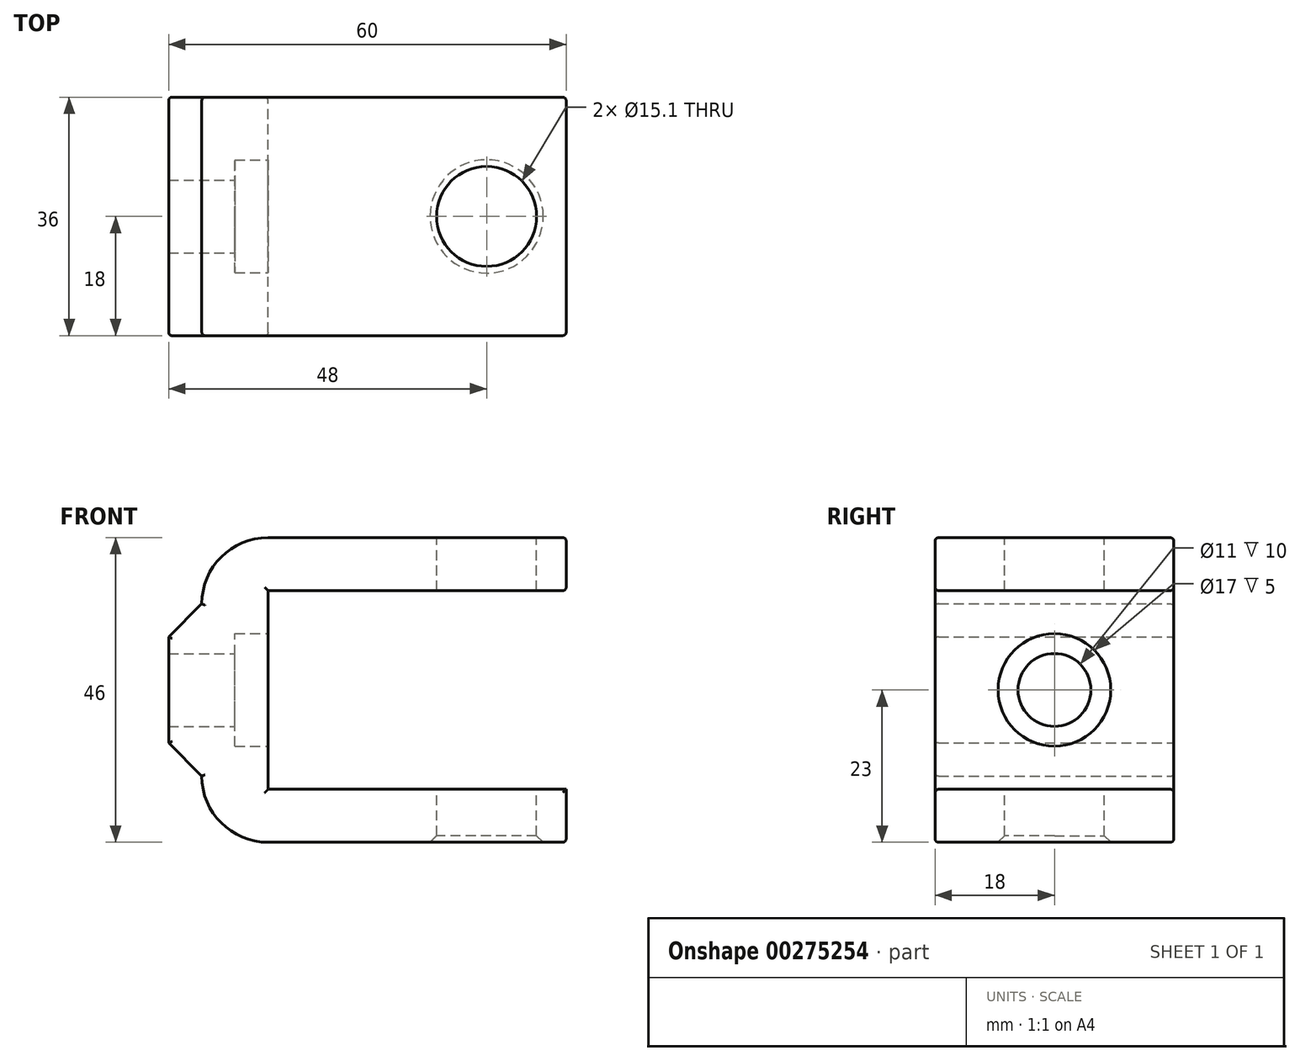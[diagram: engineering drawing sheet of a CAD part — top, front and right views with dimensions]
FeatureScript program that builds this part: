
annotation { "Feature Type Name" : "Feature", "Feature Type Description" : "" }
export const myFeature = defineFeature(function(context is Context, id is Id, definition is map)
    precondition{}
    {
        {
            var Q0;
            Q0=qCreatedBy(makeId("Front.planeOp"),FACE);
            var sketch = newSketch(context, id + "F0", { "sketchPlane" : qUnion([Q0])});
            skLineSegment(sketch, "E0", {"start": v(-43.93, 0) * mm, "end": v(68.64, 0) * mm, "construction": true});
            skLineSegment(sketch, "E1", {"start": v(0, 8) * mm, "end": v(0, -8) * mm});
            skLineSegment(sketch, "E2", {"start": v(15, 23) * mm, "end": v(60, 23) * mm});
            skLineSegment(sketch, "E3", {"start": v(60, 23) * mm, "end": v(60, 15) * mm});
            skLineSegment(sketch, "E4", {"start": v(60, 15) * mm, "end": v(22.2, 15) * mm});
            skArc(sketch, "E5", {"start": v(15, 23) * mm, "mid": v(7.93, 20.07) * mm, "end": v(5, 13) * mm});
            skLineSegment(sketch, "E6", {"start": v(15, 15) * mm, "end": v(15, -15) * mm});
            skLineSegment(sketch, "E7", {"start": v(15, -15) * mm, "end": v(60, -15) * mm});
            skLineSegment(sketch, "E8", {"start": v(60, -15) * mm, "end": v(60, -23) * mm});
            skLineSegment(sketch, "E9", {"start": v(60, -23) * mm, "end": v(15, -23) * mm});
            skLineSegment(sketch, "E10", {"start": v(15, 15) * mm, "end": v(22.2, 15) * mm});
            skArc(sketch, "E11", {"start": v(15, -23) * mm, "mid": v(7.93, -20.07) * mm, "end": v(5, -13) * mm});
            skLineSegment(sketch, "E12", {"start": v(5, 13) * mm, "end": v(5, 13) * mm});
            skLineSegment(sketch, "E13", {"start": v(5, 13) * mm, "end": v(0, 8) * mm});
            skLineSegment(sketch, "E14", {"start": v(5, -13) * mm, "end": v(5, -13) * mm});
            skLineSegment(sketch, "E15", {"start": v(5, -13) * mm, "end": v(0, -8) * mm});
            skSolve(sketch);
        }
        {
            var Q0;
            Q0=makeQuery(id+"F0.imprint","IMPRINT",FACE,{"disambiguationData":[TD([[makeQuery(id+"F0.imprint","IMPRINT",EDGE,{"derivedFrom":sQuery(id+"F0.wireOp",EDGE,"E1")}),1.0]])]});
            extrude(context, id + "F1", {"entities" : qUnion([Q0]), "endBound" : BoundingType.SYMMETRIC, "depth" : 36 * mm});
        }
        {
            var Q0;
            Q0=makeQuery(id+"F1.opExtrude","SWEPT_FACE",FACE,{"disambiguationData":[OSD([sQuery(id+"F0.wireOp",EDGE,"E2")])]});
            var sketch = newSketch(context, id + "F2", { "sketchPlane" : qUnion([Q0])});
            skCircle(sketch, "E16", {"center": v(48, 0) * mm, "radius": 7.55 * mm});
            skSolve(sketch);
        }
        {
            var Q0;
            Q0=makeQuery(id+"F2.imprint","IMPRINT",FACE,{"disambiguationData":[TD([[makeQuery(id+"F2.imprint","IMPRINT",EDGE,{"derivedFrom":sQuery(id+"F2.wireOp",EDGE,"E16")}),1.0]])]});
            extrude(context, id + "F3", {"entities" : qUnion([Q0]), "operationType" : NewBodyOperationType.REMOVE, "endBound" : BoundingType.THROUGH_ALL, "oppositeDirection" : true, "depth" : 25 * mm});
        }
        {
            var Q0;
            Q0=makeQuery(id+"F1.opExtrude","SWEPT_FACE",FACE,{"disambiguationData":[OSD([sQuery(id+"F0.wireOp",EDGE,"E6")])]});
            var sketch = newSketch(context, id + "F4", { "sketchPlane" : qUnion([Q0])});
            skPoint(sketch, "E17", {"position": v(0, 0) * mm});
            skSolve(sketch);
        }
        {
            var Q0;
            Q0=sQuery(id+"F4.wireOp",VERTEX,"E17");
            var Q1;
            Q1=makeQuery(id+"F1.opExtrude","SWEPT_BODY",BODY,{"disambiguationData":[OSD([sQuery(id+"F0.wireOp",EDGE,"E1"),sQuery(id+"F0.wireOp",EDGE,"E2"),sQuery(id+"F0.wireOp",EDGE,"E3"),sQuery(id+"F0.wireOp",EDGE,"E4"),sQuery(id+"F0.wireOp",EDGE,"E5"),sQuery(id+"F0.wireOp",EDGE,"E6"),sQuery(id+"F0.wireOp",EDGE,"E7"),sQuery(id+"F0.wireOp",EDGE,"E8"),sQuery(id+"F0.wireOp",EDGE,"E9"),sQuery(id+"F0.wireOp",EDGE,"E10"),sQuery(id+"F0.wireOp",EDGE,"E11"),sQuery(id+"F0.wireOp",EDGE,"E13"),sQuery(id+"F0.wireOp",EDGE,"E15")])]});
            hole(context, id + "F5", {"style" : HoleStyle.C_BORE, "endStyle" : HoleEndStyle.BLIND, "holeDiameter" : 11 * mm, "cBoreDiameter" : 17 * mm, "cBoreDepth" : 5 * mm, "holeDepth" : 15 * mm, "tappedDepth" : 12 * mm, "tapClearance" : 3, "locations" : qUnion([Q0]), "scope" : qUnion([Q1])});
        }
        {
            var Q0;
            Q0=makeQuery(id+"F3.boolean.opBoolean","COPY",EDGE,{"derivedFrom":makeQuery(id+"F3.opExtrude","CAP_EDGE",EDGE,{"disambiguationData":[OSD([sQuery(id+"F2.wireOp",EDGE,"E16")])],"isStart":true})});
            var Q1;
            Q1=makeQuery(id+"F3.boolean.opBoolean","INTERSECT",EDGE,{"derivedFrom":[makeQuery(id+"F1.opExtrude","SWEPT_FACE",FACE,{"disambiguationData":[OSD([sQuery(id+"F0.wireOp",EDGE,"E9")])]}),makeQuery(id+"F3.opExtrude","SWEPT_FACE",FACE,{"disambiguationData":[OSD([sQuery(id+"F2.wireOp",EDGE,"E16")])]})]});
            var Q2;
            Q2=makeQuery(id+"F5.hole-0.boolean.opBoolean","COPY",EDGE,{"derivedFrom":makeQuery(id+"F5.hole-0.opRevolve","SWEPT_EDGE",EDGE,{"disambiguationData":[OSD([sQuery(id+"F5.hole-0.sketch.wireOp",EDGE,"cbore_start_line_2"),sQuery(id+"F5.hole-0.sketch.wireOp",EDGE,"cbore_start_line_3")])]})});
            var Q3;
            Q3=makeQuery(id+"F5.hole-0.boolean.opBoolean","COPY",EDGE,{"derivedFrom":makeQuery(id+"F5.hole-0.opRevolve","SWEPT_EDGE",EDGE,{"disambiguationData":[OSD([sQuery(id+"F5.hole-0.sketch.wireOp",EDGE,"core_line_1"),sQuery(id+"F5.hole-0.sketch.wireOp",EDGE,"core_line_2")])]})});
            chamfer(context, id + "F6", {"entities" : qUnion([Q0, Q1, Q2, Q3]), "width" : 1 * mm, "tangentPropagation" : true});
        }
        {
            var Q0;
            Q0=makeQuery(id+"F1.opExtrude","SWEPT_EDGE",EDGE,{"disambiguationData":[OSD([sQuery(id+"F0.wireOp",EDGE,"E8"),sQuery(id+"F0.wireOp",EDGE,"E9")])]});
            var Q1;
            Q1=makeQuery(id+"F1.opExtrude","CAP_EDGE",EDGE,{"disambiguationData":[OSD([sQuery(id+"F0.wireOp",EDGE,"E9")])],"isStart":false});
            var Q2;
            Q2=makeQuery(id+"F1.opExtrude","CAP_EDGE",EDGE,{"disambiguationData":[OSD([sQuery(id+"F0.wireOp",EDGE,"E8")])],"isStart":false});
            var Q3;
            Q3=makeQuery(id+"F1.opExtrude","CAP_EDGE",EDGE,{"disambiguationData":[OSD([sQuery(id+"F0.wireOp",EDGE,"E7")])],"isStart":false});
            var Q4;
            Q4=makeQuery(id+"F1.opExtrude","CAP_FACE",FACE,{"disambiguationData":[OSD([sQuery(id+"F0.wireOp",EDGE,"E1"),sQuery(id+"F0.wireOp",EDGE,"E2"),sQuery(id+"F0.wireOp",EDGE,"E3"),sQuery(id+"F0.wireOp",EDGE,"E4"),sQuery(id+"F0.wireOp",EDGE,"E5"),sQuery(id+"F0.wireOp",EDGE,"E6"),sQuery(id+"F0.wireOp",EDGE,"E7"),sQuery(id+"F0.wireOp",EDGE,"E8"),sQuery(id+"F0.wireOp",EDGE,"E9"),sQuery(id+"F0.wireOp",EDGE,"E10"),sQuery(id+"F0.wireOp",EDGE,"E11"),sQuery(id+"F0.wireOp",EDGE,"E13"),sQuery(id+"F0.wireOp",EDGE,"E15")])],"isStart":false});
            var Q5;
            Q5=makeQuery(id+"F1.opExtrude","CAP_FACE",FACE,{"disambiguationData":[OSD([sQuery(id+"F0.wireOp",EDGE,"E1"),sQuery(id+"F0.wireOp",EDGE,"E2"),sQuery(id+"F0.wireOp",EDGE,"E3"),sQuery(id+"F0.wireOp",EDGE,"E4"),sQuery(id+"F0.wireOp",EDGE,"E5"),sQuery(id+"F0.wireOp",EDGE,"E6"),sQuery(id+"F0.wireOp",EDGE,"E7"),sQuery(id+"F0.wireOp",EDGE,"E8"),sQuery(id+"F0.wireOp",EDGE,"E9"),sQuery(id+"F0.wireOp",EDGE,"E10"),sQuery(id+"F0.wireOp",EDGE,"E11"),sQuery(id+"F0.wireOp",EDGE,"E13"),sQuery(id+"F0.wireOp",EDGE,"E15")])],"isStart":true});
            var Q6;
            Q6=makeQuery(id+"F1.opExtrude","SWEPT_FACE",FACE,{"disambiguationData":[OSD([sQuery(id+"F0.wireOp",EDGE,"E3")])]});
            fillet(context, id + "F7", {"entities" : qUnion([Q0, Q1, Q2, Q3, Q4, Q5, Q6]), "radius" : 0.5 * mm, "tangentPropagation" : true, "allowEdgeOverflow" : false});
        }
    });
